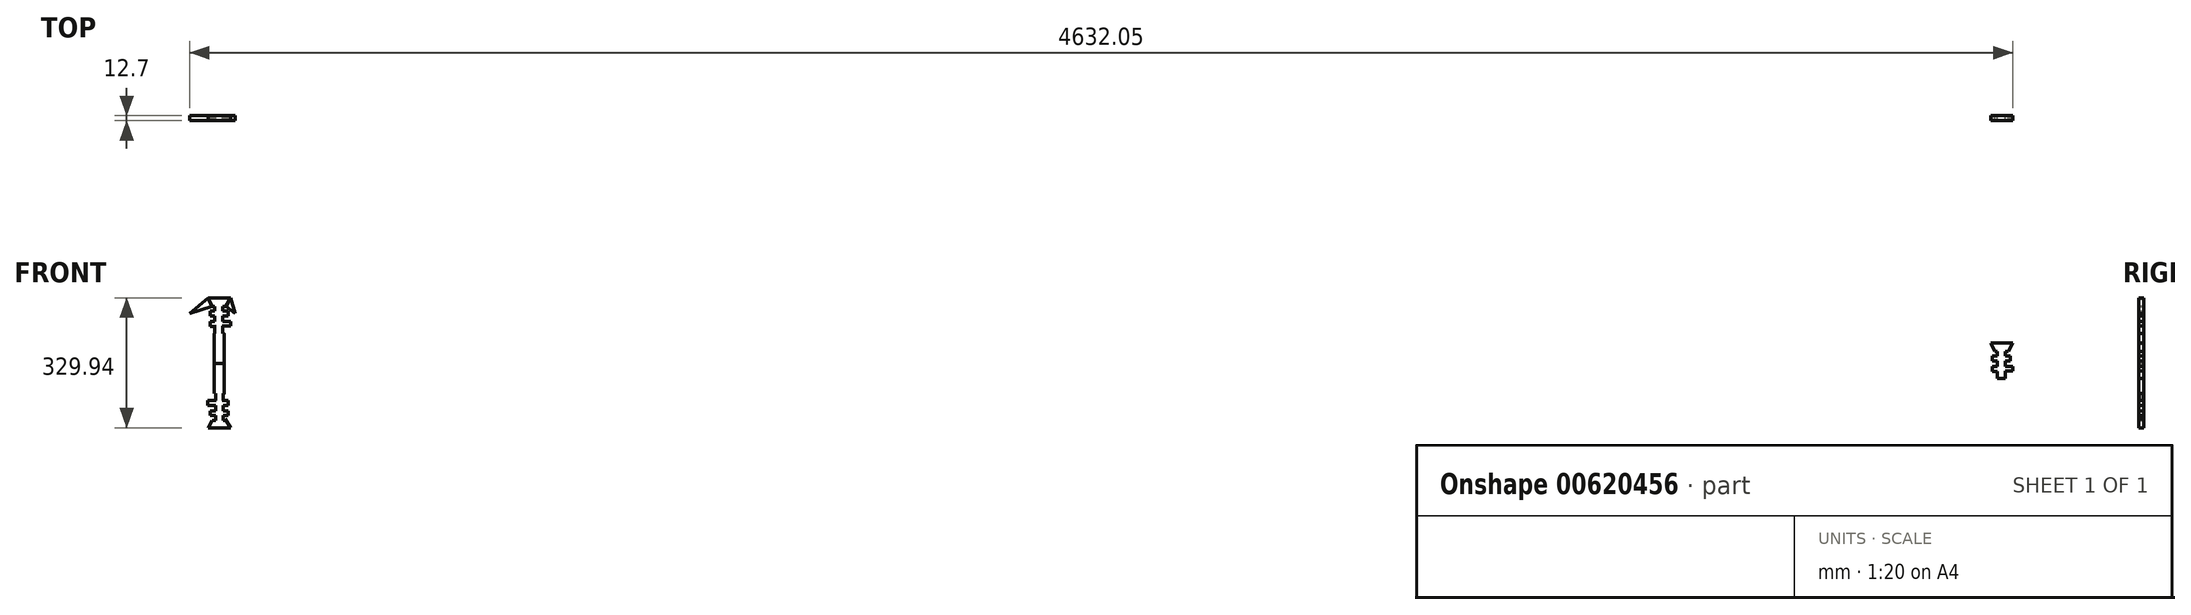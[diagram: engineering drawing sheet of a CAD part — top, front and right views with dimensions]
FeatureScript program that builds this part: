
annotation { "Feature Type Name" : "Feature", "Feature Type Description" : "" }
export const myFeature = defineFeature(function(context is Context, id is Id, definition is map)
    precondition{}
    {
        {
            var Q0;
            Q0=qCreatedBy(makeId("Front.planeOp"),FACE);
            var sketch = newSketch(context, id + "F0", { "sketchPlane" : qUnion([Q0])});
            skLineSegment(sketch, "E0", {"start": v(-24.87, 64.05) * mm, "end": v(31.59, 64.05) * mm});
            skLineSegment(sketch, "E1", {"start": v(31.59, 64.05) * mm, "end": v(19.65, 42.02) * mm});
            skLineSegment(sketch, "E2", {"start": v(19.65, 42.02) * mm, "end": v(-14.77, 42.02) * mm});
            skLineSegment(sketch, "E3", {"start": v(-14.77, 42.02) * mm, "end": v(-23.5, 61.76) * mm});
            skLineSegment(sketch, "E4", {"start": v(-8.35, 42.02) * mm, "end": v(-8.35, 30.23) * mm});
            skLineSegment(sketch, "E5", {"start": v(-8.35, 30.23) * mm, "end": v(-20.74, 30.23) * mm});
            skLineSegment(sketch, "E6", {"start": v(-20.74, 30.23) * mm, "end": v(-20.74, 18.3) * mm});
            skLineSegment(sketch, "E7", {"start": v(-20.74, 18.3) * mm, "end": v(-8.35, 18.3) * mm});
            skLineSegment(sketch, "E8", {"start": v(-8.35, 18.3) * mm, "end": v(-8.35, 4.07) * mm});
            skLineSegment(sketch, "E9", {"start": v(-8.35, 4.07) * mm, "end": v(-20.74, 4.07) * mm});
            skLineSegment(sketch, "E10", {"start": v(-20.74, 4.07) * mm, "end": v(-20.74, -8.33) * mm});
            skLineSegment(sketch, "E11", {"start": v(-20.74, -8.33) * mm, "end": v(-8.35, -8.33) * mm});
            skLineSegment(sketch, "E12", {"start": v(-8.35, -8.33) * mm, "end": v(-8.35, -26.23) * mm});
            skLineSegment(sketch, "E13", {"start": v(-8.35, -26.23) * mm, "end": v(11.85, -26.23) * mm});
            skLineSegment(sketch, "E14", {"start": v(11.85, -26.23) * mm, "end": v(11.85, -7.87) * mm});
            skLineSegment(sketch, "E15", {"start": v(11.85, -7.87) * mm, "end": v(31.59, -7.87) * mm});
            skLineSegment(sketch, "E16", {"start": v(31.59, -7.87) * mm, "end": v(31.59, 4.07) * mm});
            skLineSegment(sketch, "E17", {"start": v(31.59, 4.07) * mm, "end": v(11.85, 4.07) * mm});
            skLineSegment(sketch, "E18", {"start": v(11.85, 4.07) * mm, "end": v(11.85, 18.3) * mm});
            skLineSegment(sketch, "E19", {"start": v(11.85, 18.3) * mm, "end": v(25.16, 18.3) * mm});
            skLineSegment(sketch, "E20", {"start": v(25.16, 18.3) * mm, "end": v(25.16, 30.23) * mm});
            skLineSegment(sketch, "E21", {"start": v(25.16, 30.23) * mm, "end": v(11.85, 30.23) * mm});
            skLineSegment(sketch, "E22", {"start": v(11.85, 30.23) * mm, "end": v(11.85, 42.02) * mm});
            skLineSegment(sketch, "E23", {"start": v(-8.35, -26.23) * mm, "end": v(-10.37, -26.23) * mm});
            skLineSegment(sketch, "E24", {"start": v(-10.37, -26.23) * mm, "end": v(-10.37, -64.33) * mm});
            skLineSegment(sketch, "E25", {"start": v(-10.37, -64.33) * mm, "end": v(15.03, -64.33) * mm});
            skLineSegment(sketch, "E26", {"start": v(15.03, -64.33) * mm, "end": v(15.03, -26.23) * mm});
            skLineSegment(sketch, "E27", {"start": v(15.03, -26.23) * mm, "end": v(11.85, -26.23) * mm});
            skLineSegment(sketch, "E28", {"start": v(-24.87, 64.05) * mm, "end": v(-23.5, 61.76) * mm});
            skPoint(sketch, "E29.oppositeSnap0", {"position": v(-10.37, -45.28) * mm});
            skLineSegment(sketch, "E29.bottom", {"start": v(15.03, -64.33) * mm, "end": v(-10.37, -64.33) * mm});
            skLineSegment(sketch, "E29.top", {"start": v(15.03, -102.43) * mm, "end": v(-10.37, -102.43) * mm});
            skLineSegment(sketch, "E29.left", {"start": v(15.03, -64.33) * mm, "end": v(15.03, -102.43) * mm});
            skLineSegment(sketch, "E29.right", {"start": v(-10.37, -64.33) * mm, "end": v(-10.37, -102.43) * mm});
            skLineSegment(sketch, "E30", {"start": v(4503.1, -50.32) * mm, "end": v(4559.56, -50.32) * mm});
            skLineSegment(sketch, "E31", {"start": v(4559.56, -50.32) * mm, "end": v(4547.63, -72.35) * mm});
            skLineSegment(sketch, "E32", {"start": v(4547.63, -72.35) * mm, "end": v(4513.2, -72.35) * mm});
            skLineSegment(sketch, "E33", {"start": v(4513.2, -72.35) * mm, "end": v(4504.48, -52.61) * mm});
            skLineSegment(sketch, "E34", {"start": v(4519.62, -72.35) * mm, "end": v(4519.62, -84.13) * mm});
            skLineSegment(sketch, "E35", {"start": v(4519.62, -84.13) * mm, "end": v(4507.23, -84.13) * mm});
            skLineSegment(sketch, "E36", {"start": v(4507.23, -84.13) * mm, "end": v(4507.23, -96.07) * mm});
            skLineSegment(sketch, "E37", {"start": v(4507.23, -96.07) * mm, "end": v(4519.62, -96.07) * mm});
            skLineSegment(sketch, "E38", {"start": v(4519.62, -96.07) * mm, "end": v(4519.62, -110.3) * mm});
            skLineSegment(sketch, "E39", {"start": v(4519.62, -110.3) * mm, "end": v(4507.23, -110.3) * mm});
            skLineSegment(sketch, "E40", {"start": v(4507.23, -110.3) * mm, "end": v(4507.23, -122.7) * mm});
            skLineSegment(sketch, "E41", {"start": v(4507.23, -122.7) * mm, "end": v(4519.62, -122.7) * mm});
            skLineSegment(sketch, "E42", {"start": v(4519.62, -122.7) * mm, "end": v(4519.62, -140.6) * mm});
            skLineSegment(sketch, "E43", {"start": v(4519.62, -140.6) * mm, "end": v(4539.82, -140.6) * mm});
            skLineSegment(sketch, "E44", {"start": v(4539.82, -140.6) * mm, "end": v(4539.82, -122.23) * mm});
            skLineSegment(sketch, "E45", {"start": v(4539.82, -122.23) * mm, "end": v(4559.56, -122.23) * mm});
            skLineSegment(sketch, "E46", {"start": v(4559.56, -122.23) * mm, "end": v(4559.56, -110.3) * mm});
            skLineSegment(sketch, "E47", {"start": v(4559.56, -110.3) * mm, "end": v(4539.82, -110.3) * mm});
            skLineSegment(sketch, "E48", {"start": v(4539.82, -110.3) * mm, "end": v(4539.82, -96.07) * mm});
            skLineSegment(sketch, "E49", {"start": v(4539.82, -96.07) * mm, "end": v(4553.13, -96.07) * mm});
            skLineSegment(sketch, "E50", {"start": v(4553.13, -96.07) * mm, "end": v(4553.13, -84.13) * mm});
            skLineSegment(sketch, "E51", {"start": v(4553.13, -84.13) * mm, "end": v(4539.82, -84.13) * mm});
            skLineSegment(sketch, "E52", {"start": v(4539.82, -84.13) * mm, "end": v(4539.82, -72.35) * mm});
            skLineSegment(sketch, "E53", {"start": v(4519.62, -140.6) * mm, "end": v(4517.6, -140.6) * mm});
            skLineSegment(sketch, "E54", {"start": v(4517.6, -140.6) * mm, "end": v(4517.6, -178.7) * mm});
            skLineSegment(sketch, "E55", {"start": v(4543, -178.7) * mm, "end": v(4543, -140.6) * mm});
            skLineSegment(sketch, "E56", {"start": v(4543, -140.6) * mm, "end": v(4539.82, -140.6) * mm});
            skLineSegment(sketch, "E57", {"start": v(4503.1, -50.32) * mm, "end": v(4504.48, -52.61) * mm});
            skLineSegment(sketch, "E58.top", {"start": v(4543, -216.8) * mm, "end": v(4517.6, -216.8) * mm});
            skLineSegment(sketch, "E59", {"start": v(31.59, -265.89) * mm, "end": v(-24.87, -265.89) * mm});
            skLineSegment(sketch, "E60", {"start": v(-24.87, -265.89) * mm, "end": v(-14.65, -247.01) * mm});
            skLineSegment(sketch, "E61", {"start": v(-14.65, -247.01) * mm, "end": v(19.78, -247.01) * mm});
            skLineSegment(sketch, "E62", {"start": v(18.42, -243.94) * mm, "end": v(19.78, -247.01) * mm});
            skLineSegment(sketch, "E63", {"start": v(13.35, -247.01) * mm, "end": v(13.35, -235.22) * mm});
            skLineSegment(sketch, "E64", {"start": v(13.35, -235.22) * mm, "end": v(25.75, -235.22) * mm});
            skLineSegment(sketch, "E65", {"start": v(25.75, -235.22) * mm, "end": v(25.75, -223.29) * mm});
            skLineSegment(sketch, "E66", {"start": v(25.75, -223.29) * mm, "end": v(13.35, -223.29) * mm});
            skLineSegment(sketch, "E67", {"start": v(13.35, -223.29) * mm, "end": v(13.35, -209.06) * mm});
            skLineSegment(sketch, "E68", {"start": v(13.35, -209.06) * mm, "end": v(25.75, -209.06) * mm});
            skLineSegment(sketch, "E69", {"start": v(25.75, -209.06) * mm, "end": v(25.75, -196.67) * mm});
            skLineSegment(sketch, "E70", {"start": v(25.75, -196.67) * mm, "end": v(13.35, -196.67) * mm});
            skLineSegment(sketch, "E71", {"start": v(13.35, -196.67) * mm, "end": v(13.35, -178.76) * mm});
            skLineSegment(sketch, "E72", {"start": v(13.35, -178.76) * mm, "end": v(-6.85, -178.76) * mm});
            skLineSegment(sketch, "E73", {"start": v(-6.85, -178.76) * mm, "end": v(-6.85, -197.12) * mm});
            skLineSegment(sketch, "E74", {"start": v(-6.85, -197.12) * mm, "end": v(-26.58, -197.12) * mm});
            skLineSegment(sketch, "E75", {"start": v(-26.58, -197.12) * mm, "end": v(-26.58, -209.06) * mm});
            skLineSegment(sketch, "E76", {"start": v(-26.58, -209.06) * mm, "end": v(-6.85, -209.06) * mm});
            skLineSegment(sketch, "E77", {"start": v(-6.85, -209.06) * mm, "end": v(-6.85, -223.29) * mm});
            skLineSegment(sketch, "E78", {"start": v(-6.85, -223.29) * mm, "end": v(-20.16, -223.29) * mm});
            skLineSegment(sketch, "E79", {"start": v(-20.16, -223.29) * mm, "end": v(-20.16, -235.22) * mm});
            skLineSegment(sketch, "E80", {"start": v(-20.16, -235.22) * mm, "end": v(-6.85, -235.22) * mm});
            skLineSegment(sketch, "E81", {"start": v(-6.85, -235.22) * mm, "end": v(-6.85, -247.01) * mm});
            skLineSegment(sketch, "E82", {"start": v(13.35, -178.76) * mm, "end": v(15.37, -178.76) * mm});
            skLineSegment(sketch, "E83", {"start": v(15.37, -178.76) * mm, "end": v(15.37, -140.66) * mm});
            skLineSegment(sketch, "E84", {"start": v(15.37, -140.66) * mm, "end": v(-10.03, -140.66) * mm});
            skLineSegment(sketch, "E85", {"start": v(-10.03, -140.66) * mm, "end": v(-10.03, -178.76) * mm});
            skLineSegment(sketch, "E86", {"start": v(-10.03, -178.76) * mm, "end": v(-6.85, -178.76) * mm});
            skLineSegment(sketch, "E87", {"start": v(31.59, -265.89) * mm, "end": v(18.42, -243.94) * mm});
            skPoint(sketch, "E88.oppositeSnap0", {"position": v(15.37, -159.71) * mm});
            skLineSegment(sketch, "E88.bottom", {"start": v(-10.03, -140.66) * mm, "end": v(15.37, -140.66) * mm});
            skLineSegment(sketch, "E88.top", {"start": v(-10.03, -102.56) * mm, "end": v(15.37, -102.56) * mm});
            skLineSegment(sketch, "E88.left", {"start": v(-10.03, -140.66) * mm, "end": v(-10.03, -102.56) * mm});
            skLineSegment(sketch, "E88.right", {"start": v(15.37, -140.66) * mm, "end": v(15.37, -102.56) * mm});
            skSolve(sketch);
        }
        {
            var Q0;
            Q0 = qSketchRegion(id + "F0", true);
            extrude(context, id + "F1", {"entities" : qUnion([Q0]), "endBound" : BoundingType.SYMMETRIC, "depth" : 12.7 * mm, "offsetDistance" : 25.4 * mm});
        }
        {
            var Q0;
            Q0=makeQuery(id+"F1.opExtrude","CAP_EDGE",EDGE,{"disambiguationData":[OSD([sQuery(id+"F0.wireOp",EDGE,"E24"),sQuery(id+"F0.wireOp",EDGE,"E29.right")])],"isStart":false});
            var Q1;
            Q1=makeQuery(id+"F1.opExtrude","CAP_EDGE",EDGE,{"disambiguationData":[OSD([sQuery(id+"F0.wireOp",EDGE,"E85"),sQuery(id+"F0.wireOp",EDGE,"E88.left")])],"isStart":false});
            var Q2;
            Q2=makeQuery(id+"F1.opExtrude","CAP_EDGE",EDGE,{"disambiguationData":[OSD([sQuery(id+"F0.wireOp",EDGE,"E83"),sQuery(id+"F0.wireOp",EDGE,"E88.right")])],"isStart":false});
            var Q3;
            Q3=makeQuery(id+"F1.opExtrude","CAP_EDGE",EDGE,{"disambiguationData":[OSD([sQuery(id+"F0.wireOp",EDGE,"E83"),sQuery(id+"F0.wireOp",EDGE,"E88.right")])],"isStart":true});
            var Q4;
            Q4=makeQuery(id+"F1.opExtrude","CAP_EDGE",EDGE,{"disambiguationData":[OSD([sQuery(id+"F0.wireOp",EDGE,"E26"),sQuery(id+"F0.wireOp",EDGE,"E29.left")])],"isStart":true});
            var Q5;
            Q5=makeQuery(id+"F1.opExtrude","CAP_EDGE",EDGE,{"disambiguationData":[OSD([sQuery(id+"F0.wireOp",EDGE,"E26"),sQuery(id+"F0.wireOp",EDGE,"E29.left")])],"isStart":false});
            var Q6;
            Q6=makeQuery(id+"F1.opExtrude","CAP_EDGE",EDGE,{"disambiguationData":[OSD([sQuery(id+"F0.wireOp",EDGE,"E24"),sQuery(id+"F0.wireOp",EDGE,"E29.right")])],"isStart":true});
            var Q7;
            Q7=makeQuery(id+"F1.opExtrude","CAP_EDGE",EDGE,{"disambiguationData":[OSD([sQuery(id+"F0.wireOp",EDGE,"E85"),sQuery(id+"F0.wireOp",EDGE,"E88.left")])],"isStart":true});
            fillet(context, id + "F2", {"entities" : qUnion([Q0, Q1, Q2, Q3, Q4, Q5, Q6, Q7]), "radius" : 5.08 * mm, "tangentPropagation" : true, "allowEdgeOverflow" : false});
        }
        {
            var Q0;
            Q0=qCreatedBy(makeId("Front.planeOp"),FACE);
            var sketch = newSketch(context, id + "F3", { "sketchPlane" : qUnion([Q0])});
            skLineSegment(sketch, "E89", {"start": v(-24.83, 63.32) * mm, "end": v(-72.5, 24.5) * mm});
            skLineSegment(sketch, "E90", {"start": v(-72.5, 24.5) * mm, "end": v(-15.97, 42.21) * mm});
            skLineSegment(sketch, "E91", {"start": v(-15.97, 42.21) * mm, "end": v(-24.83, 63.32) * mm});
            skLineSegment(sketch, "E92", {"start": v(20.12, 42.21) * mm, "end": v(43.27, 24.5) * mm});
            skLineSegment(sketch, "E93", {"start": v(43.27, 24.5) * mm, "end": v(31.7, 63.32) * mm});
            skLineSegment(sketch, "E94", {"start": v(31.7, 63.32) * mm, "end": v(20.12, 42.21) * mm});
            skSolve(sketch);
        }
        {
            var Q0;
            Q0=makeQuery(id+"F3.imprint","IMPRINT",FACE,{"disambiguationData":[TD([[makeQuery(id+"F3.imprint","IMPRINT",EDGE,{"derivedFrom":sQuery(id+"F3.wireOp",EDGE,"E89")}),1.0]])]});
            var Q1;
            Q1=makeQuery(id+"F3.imprint","IMPRINT",FACE,{"disambiguationData":[TD([[makeQuery(id+"F3.imprint","IMPRINT",EDGE,{"derivedFrom":sQuery(id+"F3.wireOp",EDGE,"E92")}),1.0]])]});
            extrude(context, id + "F4", {"entities" : qUnion([Q0, Q1]), "endBound" : BoundingType.SYMMETRIC, "oppositeDirection" : true, "depth" : 12.7 * mm, "offsetDistance" : 25.4 * mm});
        }
    });
